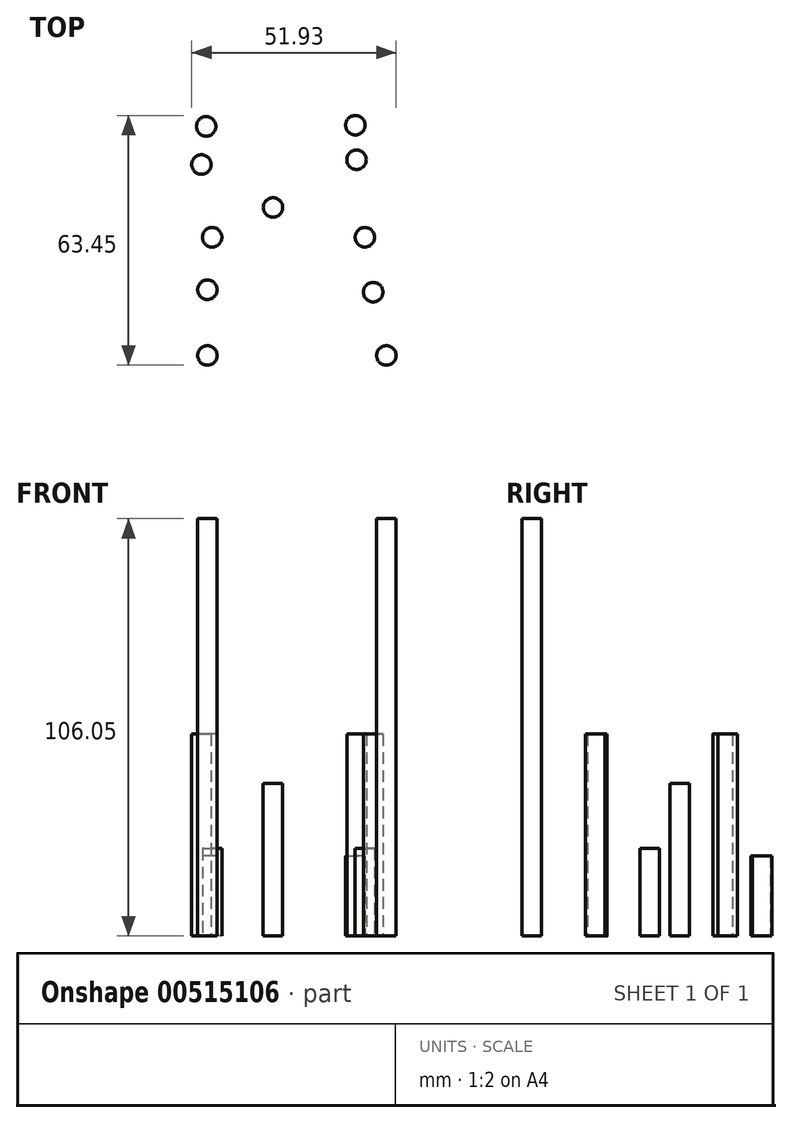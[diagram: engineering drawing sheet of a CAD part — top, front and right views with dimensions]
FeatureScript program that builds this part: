
annotation { "Feature Type Name" : "Feature", "Feature Type Description" : "" }
export const myFeature = defineFeature(function(context is Context, id is Id, definition is map)
    precondition{}
    {
        {
            var Q0;
            Q0=qCreatedBy(makeId("Top.planeOp"),FACE);
            var sketch = newSketch(context, id + "F0", { "sketchPlane" : qUnion([Q0])});
            skCircle(sketch, "E0", {"center": v(-22.12, 0) * mm, "radius": 2.48 * mm});
            skCircle(sketch, "E1", {"center": v(23.34, 0) * mm, "radius": 2.48 * mm});
            skSolve(sketch);
        }
        {
            var Q0;
            Q0 = qSketchRegion(id + "F0", true);
            extrude(context, id + "F1", {"entities" : qUnion([Q0]), "depth" : 106.04 * mm, "offsetDistance" : 25.4 * mm});
        }
        {
            var Q0;
            Q0=qCreatedBy(makeId("Top.planeOp"),FACE);
            var sketch = newSketch(context, id + "F2", { "sketchPlane" : qUnion([Q0])});
            skCircle(sketch, "E2", {"center": v(-22.12, 16.67) * mm, "radius": 2.48 * mm});
            skCircle(sketch, "E3", {"center": v(20, 16.06) * mm, "radius": 2.48 * mm});
            skSolve(sketch);
        }
        {
            var Q0;
            Q0 = qSketchRegion(id + "F2", true);
            extrude(context, id + "F3", {"entities" : qUnion([Q0]), "depth" : 51.3 * mm, "offsetDistance" : 25.4 * mm});
        }
        {
            var Q0;
            Q0=qCreatedBy(makeId("Top.planeOp"),FACE);
            var sketch = newSketch(context, id + "F4", { "sketchPlane" : qUnion([Q0])});
            skCircle(sketch, "E4", {"center": v(-20.91, 30) * mm, "radius": 2.48 * mm});
            skCircle(sketch, "E5", {"center": v(17.88, 30) * mm, "radius": 2.48 * mm});
            skSolve(sketch);
        }
        {
            var Q0;
            Q0=makeQuery(id+"F4.imprint","IMPRINT",FACE,{"disambiguationData":[TD([[makeQuery(id+"F4.imprint","IMPRINT",EDGE,{"derivedFrom":sQuery(id+"F4.wireOp",EDGE,"E4")}),1.0]])]});
            var Q1;
            Q1=makeQuery(id+"F4.imprint","IMPRINT",FACE,{"disambiguationData":[TD([[makeQuery(id+"F4.imprint","IMPRINT",EDGE,{"derivedFrom":sQuery(id+"F4.wireOp",EDGE,"E5")}),1.0]])]});
            extrude(context, id + "F5", {"entities" : qUnion([Q0, Q1]), "depth" : 22.22 * mm, "offsetDistance" : 25.4 * mm});
        }
        {
            var Q0;
            Q0=qCreatedBy(makeId("Top.planeOp"),FACE);
            var sketch = newSketch(context, id + "F6", { "sketchPlane" : qUnion([Q0])});
            skCircle(sketch, "E6", {"center": v(-5.46, 37.58) * mm, "radius": 2.48 * mm});
            skSolve(sketch);
        }
        {
            var Q0;
            Q0=makeQuery(id+"F6.imprint","IMPRINT",FACE,{"disambiguationData":[TD([[makeQuery(id+"F6.imprint","IMPRINT",EDGE,{"derivedFrom":sQuery(id+"F6.wireOp",EDGE,"E6")}),1.0]])]});
            extrude(context, id + "F7", {"entities" : qUnion([Q0]), "depth" : 38.73 * mm, "offsetDistance" : 25.4 * mm});
        }
        {
            var Q0;
            Q0=qCreatedBy(makeId("Top.planeOp"),FACE);
            var sketch = newSketch(context, id + "F8", { "sketchPlane" : qUnion([Q0])});
            skCircle(sketch, "E7", {"center": v(-23.64, 48.5) * mm, "radius": 2.48 * mm});
            skCircle(sketch, "E8", {"center": v(15.76, 49.7) * mm, "radius": 2.48 * mm});
            skSolve(sketch);
        }
        {
            var Q0;
            Q0=makeQuery(id+"F8.imprint","IMPRINT",FACE,{"disambiguationData":[TD([[makeQuery(id+"F8.imprint","IMPRINT",EDGE,{"derivedFrom":sQuery(id+"F8.wireOp",EDGE,"E7")}),1.0]])]});
            var Q1;
            Q1=makeQuery(id+"F8.imprint","IMPRINT",FACE,{"disambiguationData":[TD([[makeQuery(id+"F8.imprint","IMPRINT",EDGE,{"derivedFrom":sQuery(id+"F8.wireOp",EDGE,"E8")}),1.0]])]});
            extrude(context, id + "F9", {"entities" : qUnion([Q0, Q1]), "depth" : 51.3 * mm, "offsetDistance" : 25.4 * mm});
        }
        {
            var Q0;
            Q0=qCreatedBy(makeId("Top.planeOp"),FACE);
            var sketch = newSketch(context, id + "F10", { "sketchPlane" : qUnion([Q0])});
            skCircle(sketch, "E9", {"center": v(-22.43, 58.19) * mm, "radius": 2.48 * mm});
            skCircle(sketch, "E10", {"center": v(15.46, 58.5) * mm, "radius": 2.48 * mm});
            skSolve(sketch);
        }
        {
            var Q0;
            Q0=makeQuery(id+"F10.imprint","IMPRINT",FACE,{"disambiguationData":[TD([[makeQuery(id+"F10.imprint","IMPRINT",EDGE,{"derivedFrom":sQuery(id+"F10.wireOp",EDGE,"E9")}),1.0]])]});
            var Q1;
            Q1=makeQuery(id+"F10.imprint","IMPRINT",FACE,{"disambiguationData":[TD([[makeQuery(id+"F10.imprint","IMPRINT",EDGE,{"derivedFrom":sQuery(id+"F10.wireOp",EDGE,"E10")}),1.0]])]});
            extrude(context, id + "F11", {"entities" : qUnion([Q0, Q1]), "depth" : 20.32 * mm, "offsetDistance" : 25.4 * mm});
        }
    });
